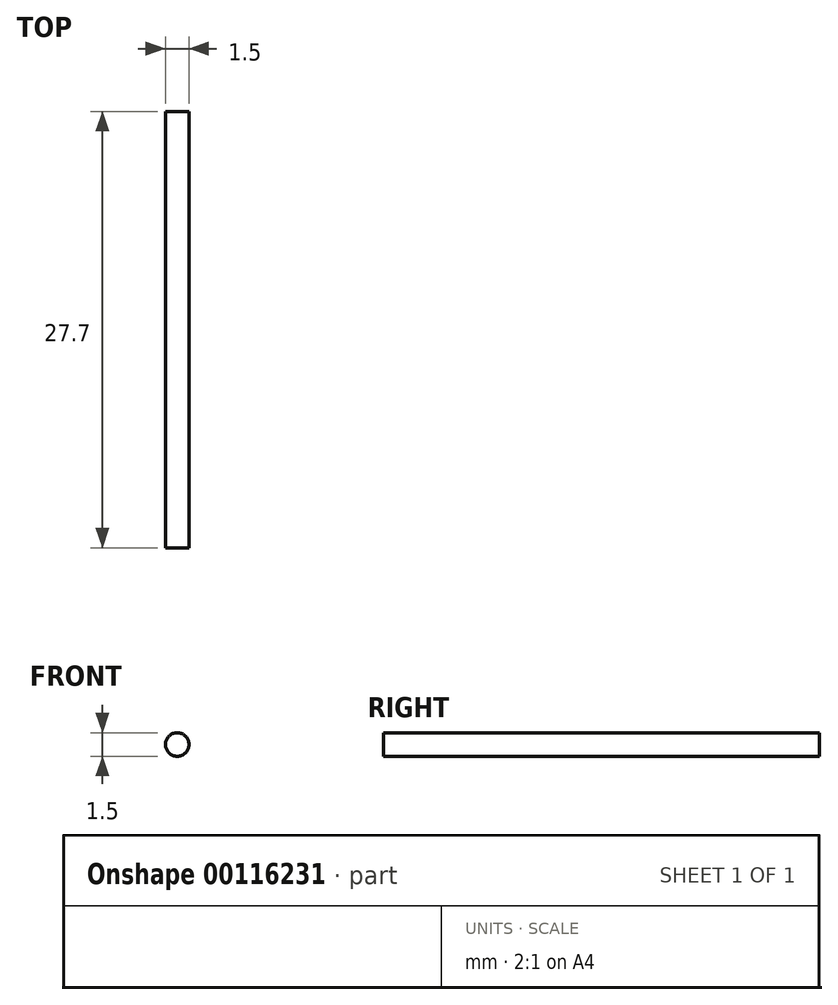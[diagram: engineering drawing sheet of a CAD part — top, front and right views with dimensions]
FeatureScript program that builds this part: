
annotation { "Feature Type Name" : "Feature", "Feature Type Description" : "" }
export const myFeature = defineFeature(function(context is Context, id is Id, definition is map)
    precondition{}
    {
        {
            var Q0;
            Q0=qCreatedBy(makeId("Front.planeOp"),FACE);
            var sketch = newSketch(context, id + "F0", { "sketchPlane" : qUnion([Q0])});
            skCircle(sketch, "E0", {"center": v(0, 0) * mm, "radius": 0.75 * mm});
            skSolve(sketch);
        }
        {
            var Q0;
            Q0 = qSketchRegion(id + "F0", true);
            extrude(context, id + "F1", {"entities" : qUnion([Q0]), "depth" : 27.7 * mm, "symmetric" : true});
        }
    });
